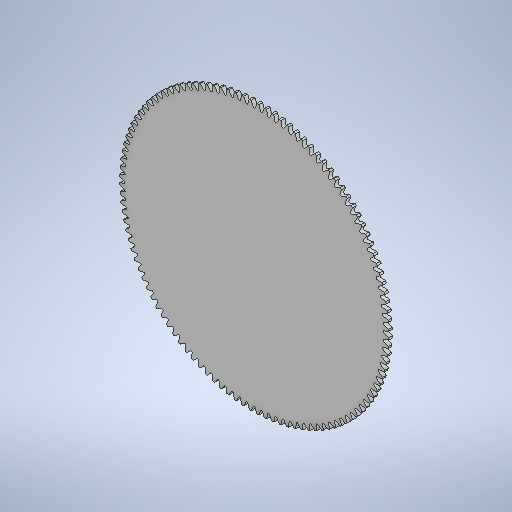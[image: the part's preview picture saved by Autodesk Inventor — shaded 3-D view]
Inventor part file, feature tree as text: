
AUTODESK INVENTOR PART (.ipt)
format: ipt  version: 2025 (Build 290162010, 162A)  size: 939,008 bytes
history: native  units: mm
features: extrude x3, pattern_circular x1, sketch x1, projected_geometry x1
ambient origin geometry x8: Origin, YZ Plane, XZ Plane, XY Plane, X Axis, Y Axis, Z Axis, Center Point
bodies: Solid1 (feature_tree)
feature tree (6):
  extrude  "Extrusion1"  TaperAngle=0.0deg  [1 undecoded]
  extrude  "Extrusion2"  TaperAngle=0.0deg  [1 undecoded]
  pattern_circular  "Circular Pattern1"  Count=112 Angle=360.0deg
  extrude  "Extrusion3"  Depth=720.0mm
  sketch  "Sketch2"  dims[d0=20.0mm d1=0.0mm d2=0.0mm d3=0.0mm d4=1120.0mm d5=360.0deg d7=720.0mm d8=2.243998mm d9=0.0mm d10=0.0mm]
  projected_geometry  "Projected Loop1"
note: 2 required parameter values undecoded (feature->parameter linkage not recoverable at this tier; creation-order binding heuristic only, values carry confidence <= 0.55)
